# Revit family: DT6
name_source: partatom
category: Communication Devices
revit_build: Autodesk Revit 2014 (Build: 20130308_1515(x64)
units: mm (PartAtom-declared; Revit-internal decimal feet)

## types (1)
- DT6
    25V Taps = .25, .5, 1, 2, & .4 Watts
    Baffle Material = <By Category>
    Body Material = QF_Plastic - White - Smooth
    Color = <By Category>
    Cost = 0 $
    Cost MSRP = 55.99 $
    Default Elevation = 48 "
    Depth = 4.2 "
    Description = 6" X 2' DROP TILE SPEAKER PACKAGE
    Enclosure Material = <By Category>
    Family Code (default) = ITS Inc.
    Frequency Response  = 125Hz-8kHz (+/-6dB)
    Grill Material = <By Category>
    Height = 23.9 "
    Horizontal Symmetry = No
    IQ Category = SPEAKERS
    Ingress Protection = IP-21
    Manufacturer = ATLAS SOUND
    Manufacturer URL = https://www.atlasied.com
    Market = Commercial, Higher Education, Emergency
    MasterFormat = 27 41 13
    Model = DT6
    Mount Material = Default
    OmniClass Number = 23-37 17 13 19
    OmniClass Title = SPEAKERS
    Part Number = DT6
    Power Rating (RMS) = 10 Watts
    Product Documentation Link = https://www.atlasied.com
    Product Page URL = https://www.atlasied.com
    Safety Agency Ratings = UL Listed to Comply with UL1480, UL2043
    ScheduleType |RF| = AtlasIED Master
    Sensitivity = 87
    Speaker Height = 120 "
    Speaker Listening Height = 30 "
    Type Driver = 3" Cone Type
    URL = www.atlassound.com
    Vertical Symmetry = No
    Warranty = TBD
    Weight in Pounds = 4.2
    Width = 5.97 "

## geometry (parser evidence)
native form markers: Sweep x4
no freeform markers — native parametric forms only
